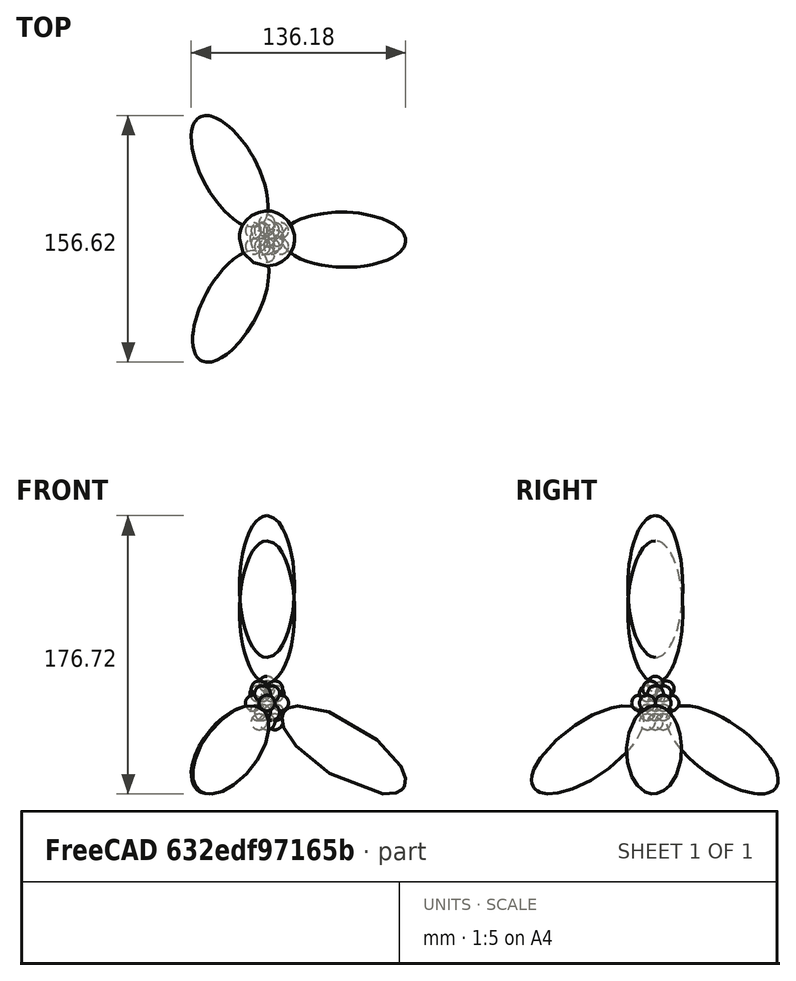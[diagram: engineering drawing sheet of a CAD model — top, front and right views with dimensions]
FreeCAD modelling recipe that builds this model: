
FCSTD DOCUMENT  (FreeCAD 0.16R6707 (Git))
Label: si-atom
License: All rights reserved
LicenseURL: http://en.wikipedia.org/wiki/All_rights_reserved
objects: Part::Feature×23, Part::Part2DObjectPython×15, Part::Sphere×9, App::DocumentObjectGroup×5, Sketcher::SketchObject×1, PartDesign::Revolution×1
note: 50 computed .brp shape members not serialized (recipe doc carries the construction recipe); baked Part::Feature solids carry a one-line shape summary decoded from their .brp

FEATURE [Part::Feature] Sphere001
  Placement = pos=(0,-10,31) rot=(0,0,1;0rad)
  shape: bbox 10 x 10 x 10 mm, 1 faces (baked)
FEATURE [Part::Feature] Sphere002
  Placement = pos=(-8.66025,-5,31) rot=(0,0,1;0rad)
  shape: bbox 10 x 10 x 10 mm, 1 faces (baked)
FEATURE [Part::Feature] Sphere003
  Placement = pos=(-8.66025,5,31) rot=(0,0,1;0rad)
  shape: bbox 10 x 10 x 10 mm, 1 faces (baked)
FEATURE [Part::Feature] Sphere004
  Placement = pos=(8.66025,-5,31) rot=(0,0,1;0rad)
  shape: bbox 10 x 10 x 10 mm, 1 faces (baked)
FEATURE [Part::Feature] Sphere005
  Placement = pos=(8.66025,5,31) rot=(0,0,1;0rad)
  shape: bbox 10 x 10 x 10 mm, 1 faces (baked)
FEATURE [Part::Feature] Sphere006
  Placement = pos=(4e-12,10,31) rot=(0,0,1;0rad)
  shape: bbox 10 x 10 x 10 mm, 1 faces (baked)
FEATURE [Part::Sphere] Sphere007
  Angle1 = -90
  Angle2 = 90
  Angle3 = 360
  Placement = pos=(0,0,31) rot=(0,0,1;0rad)
  Radius = 5
FEATURE [Part::Feature] Sphere  label="Sphere027"
  Placement = pos=(-3,5,37) rot=(0,0,1;0rad)
  shape: bbox 10 x 10 x 10 mm, 1 faces (baked)
FEATURE [Part::Feature] Sphere008  label="Sphere028"
  Placement = pos=(2.83013,5.09808,37) rot=(0,0,1;0rad)
  shape: bbox 10 x 10 x 10 mm, 1 faces (baked)
FEATURE [Part::Feature] Sphere009  label="Sphere029"
  Placement = pos=(5.83013,0.0980762,37) rot=(0,0,1;0rad)
  shape: bbox 10 x 10 x 10 mm, 1 faces (baked)
FEATURE [Part::Feature] Sphere010  label="Sphere030"
  Placement = pos=(3,-5,37) rot=(0,0,1;0rad)
  shape: bbox 10 x 10 x 10 mm, 1 faces (baked)
FEATURE [Part::Feature] Sphere011  label="Sphere031"
  Placement = pos=(-2.83013,-5.09808,37) rot=(0,0,1;0rad)
  shape: bbox 10 x 10 x 10 mm, 1 faces (baked)
FEATURE [Part::Feature] Sphere012  label="Sphere032"
  Placement = pos=(-5.83013,-0.0980762,37) rot=(0,0,1;0rad)
  shape: bbox 10 x 10 x 10 mm, 1 faces (baked)
FEATURE [Part::Feature] Sphere013  label="Sphere033"
  Placement = pos=(-3,5,25) rot=(0,0,1;0rad)
  shape: bbox 10 x 10 x 10 mm, 1 faces (baked)
FEATURE [Part::Feature] Sphere014  label="Sphere034"
  Placement = pos=(2.83013,5.09808,25) rot=(0,0,1;0rad)
  shape: bbox 10 x 10 x 10 mm, 1 faces (baked)
FEATURE [Part::Feature] Sphere015  label="Sphere035"
  Placement = pos=(-2.83013,-5.09808,25) rot=(0,0,1;0rad)
  shape: bbox 10 x 10 x 10 mm, 1 faces (baked)
FEATURE [Part::Feature] Sphere016  label="Sphere036"
  Placement = pos=(5.83013,0.0980762,25) rot=(0,0,1;0rad)
  shape: bbox 10 x 10 x 10 mm, 1 faces (baked)
FEATURE [Part::Feature] Sphere017  label="Sphere015"
  Placement = pos=(3,-5,25) rot=(0,0,1;0rad)
  shape: bbox 10 x 10 x 10 mm, 1 faces (baked)
FEATURE [Part::Feature] Sphere018  label="Sphere037"
  Placement = pos=(-5.83013,-0.0980762,25) rot=(0,0,1;0rad)
  shape: bbox 10 x 10 x 10 mm, 1 faces (baked)
FEATURE [Part::Sphere] Sphere019
  Angle1 = -90
  Angle2 = 90
  Angle3 = 360
  Placement = pos=(0,0,43) rot=(0,0,1;0rad)
  Radius = 5
FEATURE [Part::Sphere] Sphere020  label="Sphere038"
  Angle1 = -90
  Angle2 = 90
  Angle3 = 360
  Placement = pos=(0,0,19) rot=(0,0,1;0rad)
  Radius = 5
FEATURE [Part::Sphere] Sphere021  label="Sphere039"
  Angle1 = -90
  Angle2 = 90
  Angle3 = 360
  Placement = pos=(0,7,40) rot=(0,0,1;0rad)
  Radius = 5
FEATURE [Part::Sphere] Sphere022  label="Sphere040"
  Angle1 = -90
  Angle2 = 90
  Angle3 = 360
  Placement = pos=(-5,-3,40) rot=(0,0,1;0rad)
  Radius = 5
FEATURE [Part::Sphere] Sphere023  label="Sphere041"
  Angle1 = -90
  Angle2 = 90
  Angle3 = 360
  Placement = pos=(5,-3,40) rot=(0,0,1;0rad)
  Radius = 5
FEATURE [Part::Sphere] Sphere024  label="Sphere042"
  Angle1 = -90
  Angle2 = 90
  Angle3 = 360
  Placement = pos=(-5,5,19) rot=(0,0,1;0rad)
  Radius = 5
FEATURE [Part::Sphere] Sphere025  label="Sphere043"
  Angle1 = -90
  Angle2 = 90
  Angle3 = 360
  Placement = pos=(5,5,19) rot=(0,0,1;0rad)
  Radius = 5
FEATURE [Part::Sphere] Sphere026  label="Sphere044"
  Angle1 = -90
  Angle2 = 90
  Angle3 = 360
  Placement = pos=(0,-5,19) rot=(0,0,1;0rad)
  Radius = 5
FEATURE [App::DocumentObjectGroup] Group  label="core"
  Group = -> [Sphere001,Sphere002,Sphere003,Sphere004,Sphere005,Sphere006,Sphere007,Sphere,Sphere008,Sphere009,Sphere010,Sphere011,Sphere012,Sphere013,Sphere014,Sphere015,Sphere016,Sphere017,Sphere018,Sphere019,Sphere020,Sphere021,Sphere022,Sphere023,Sphere024,Sphere025,Sphere026]
FEATURE [Part::Part2DObjectPython] Polygon  # Draft 2D object (typed FeaturePython)
  ChamferSize = 0
  DrawMode = 0
  FacesNumber = 3
  FilletRadius = 0
  MakeFace = false
  Radius = 50
FEATURE [Part::Part2DObjectPython] Line  # Draft 2D object (typed FeaturePython)
  ChamferSize = 0
  Closed = false
  End = (0.452401,-0.175885,80)
  FilletRadius = 0
  Length = 80
  MakeFace = true
  Points = (2) [(0.452401,-0.175885,0),(0.452401,-0.175885,80)]
  Start = (0.452401,-0.175885,0)
  Subdivisions = 0
FEATURE [Part::Part2DObjectPython] Arc  # Draft 2D object (typed FeaturePython)
  FirstAngle = -171.133
  LastAngle = -90
  MakeFace = true
  Placement = pos=(-25,43.3013,0) rot=(0,0,1;0rad)
  Radius = 86.6025
FEATURE [Part::Part2DObjectPython] Arc001  # Draft 2D object (typed FeaturePython)
  FirstAngle = 90
  LastAngle = 169.455
  MakeFace = true
  Placement = pos=(-25,-43.3013,0) rot=(0,0,1;0rad)
  Radius = 86.6025
FEATURE [Part::Part2DObjectPython] Line001  # Draft 2D object (typed FeaturePython)
  ChamferSize = 0
  Closed = false
  End = (-25,0,0)
  FilletRadius = 0
  Length = 75
  MakeFace = true
  Points = (2) [(-100,0,0),(-25,-2.13163e-14,0)]
  Start = (-100,0,0)
  Subdivisions = 0
FEATURE [Part::Part2DObjectPython] Arc002  # Draft 2D object (typed FeaturePython)
  FirstAngle = 52.9075
  LastAngle = 180
  MakeFace = true
  Placement = pos=(-25,0,0) rot=(1,0,0;1.5708rad)
  Radius = 75
FEATURE [Part::Part2DObjectPython] Line002  # Draft 2D object (typed FeaturePython)
  ChamferSize = 0
  Closed = false
  End = (-25,-43.3013,0)
  FilletRadius = 0
  Length = 87.0816
  MakeFace = true
  Points = (2) [(1.07885,0,70.9091),(-25,-43.3013,0)]
  Start = (1.07885,0,70.9091)
  Subdivisions = 0
FEATURE [Part::Part2DObjectPython] Line003  # Draft 2D object (typed FeaturePython)
  ChamferSize = 0
  Closed = false
  End = (50,0,0)
  FilletRadius = 0
  Length = 86.1474
  MakeFace = true
  Points = (2) [(1.07885,0,70.9091),(50,1.53081e-15,0)]
  Start = (1.07885,0,70.9091)
  Subdivisions = 0
FEATURE [Part::Part2DObjectPython] Line004  # Draft 2D object (typed FeaturePython)
  ChamferSize = 0
  Closed = false
  End = (-25,43.3013,0)
  FilletRadius = 0
  Length = 87.0816
  MakeFace = true
  Points = (2) [(1.07885,0,70.9091),(-25,43.3013,0)]
  Start = (1.07885,0,70.9091)
  Subdivisions = 0
FEATURE [App::DocumentObjectGroup] Group001  label="tetrahedron"
  Group = -> [Line002,Line003,Line004,Polygon]
FEATURE [Part::Part2DObjectPython] Line006  # Draft 2D object (typed FeaturePython)
  ChamferSize = 0
  Closed = false
  End = (50,0,0)
  FilletRadius = 0
  Length = 58.8303
  MakeFace = true
  Points = (2) [(0,0,31),(50,1.53081e-15,0)]
  Start = (0,0,31)
  Subdivisions = 0
FEATURE [Part::Part2DObjectPython] Line007  # Draft 2D object (typed FeaturePython)
  ChamferSize = 0
  Closed = false
  End = (1.07885,0,70.9091)
  FilletRadius = 0
  Length = 39.9237
  MakeFace = true
  Points = (2) [(0,0,31),(1.07885,0,70.9091)]
  Start = (0,0,31)
  Subdivisions = 0
FEATURE [Part::Part2DObjectPython] Line008  # Draft 2D object (typed FeaturePython)
  ChamferSize = 0
  Closed = false
  End = (-25,43.3013,0)
  FilletRadius = 0
  Length = 58.8303
  MakeFace = true
  Points = (2) [(0,0,31),(-25,43.3013,0)]
  Start = (0,0,31)
  Subdivisions = 0
FEATURE [Sketcher::SketchObject] Sketch
  Placement = pos=(0,0,0) rot=(1,0,0;1.5708rad)
  sketch-geometry (6):
    g0: LineSegment StartX=0 StartY=60 StartZ=0 EndX=0 EndY=150 EndZ=0
    g1: ArcOfEllipse CenterX=0 CenterY=105 CenterZ=0 NormalX=0 NormalY=0 NormalZ=1 MajorRadius=45 MinorRadius=17.5 AngleXU=1.5708 StartAngle=3.14159 EndAngle=6.28319
    g2: LineSegment [constr] StartX=0 StartY=150 StartZ=0 EndX=0 EndY=60 EndZ=0
    g3: LineSegment [constr] StartX=-17.5 StartY=105 StartZ=0 EndX=17.5 EndY=105 EndZ=0
    g4: GeomPoint [constr] X=0 Y=146.458 Z=0
    g5: GeomPoint [constr] X=0 Y=63.5422 Z=0
  constraints (10):
    c: PointOnObject(g0,g-2)
    c: PointOnObject(g0,g-2)
    c: InternalAlignment(g2-g5 -> g1) x4
    c: Coincident(g2,g0)
    c: Coincident(g1,g0)
    c: Coincident(g2,g0)
    c: DistanceX(g3,g3) = 35
    c: DistanceY(g-1,g0) = 60
    c: DistanceY(g0,g0) = 90
    c: Coincident(g1,g0)
FEATURE [PartDesign::Revolution] Revolution001  label="orbital-1"
  Angle = 360
  Axis = (0,0,1)
  Base = (0,0,0)
  Placement = pos=(0,0,0) rot=(1,0,0;1.5708rad)
  ReferenceAxis = -> Sketch [V_Axis]
  Reversed = true
  Sketch = -> Sketch
FEATURE [Part::Feature] Face
  shape: bbox 40.2 x 69.18 x 91.71 mm, 1 faces, 0 solids (baked)
FEATURE [Part::Part2DObjectPython] Arc003  # Draft 2D object (typed FeaturePython)
  FirstAngle = -223.482
  LastAngle = -86.8237
  MakeFace = true
  Placement = pos=(0,0,31) rot=(-0.761669,-0.469136,0.446958;1.79277rad)
  Radius = 39.9237
FEATURE [Part::Part2DObjectPython] Line010  # Draft 2D object (typed FeaturePython)
  ChamferSize = 0
  Closed = false
  End = (68.0246,117.822,115.351)
  FilletRadius = 0
  Length = 200
  MakeFace = true
  Points = (2) [(-16.9656,-29.3853,9.96263),(68.0246,117.822,115.351)]
  Start = (-16.9656,-29.3853,9.96263)
  Subdivisions = 0
FEATURE [Part::Part2DObjectPython] Line005  # Draft 2D object (typed FeaturePython)
  ChamferSize = 0
  Closed = false
  End = (-25,-43.3013,0)
  FilletRadius = 0
  Length = 58.8303
  MakeFace = true
  Points = (2) [(0,0,31),(-25,-43.3013,0)]
  Start = (0,0,31)
  Subdivisions = 0
  Support = -> Sphere005
FEATURE [App::DocumentObjectGroup] Group002  label="Aux"
  Group = -> [Line,Arc,Arc001,Line001,Arc002,Line006,Line007,Line008,Face,Arc003,Line010,Line005]
FEATURE [App::DocumentObjectGroup] Group003  label="Orbital-src"
  Group = -> [Revolution001]
FEATURE [Part::Feature] Revolution001001  label="orbital-005"
  Placement = pos=(0,0,-16) rot=(1,0,0;1.5708rad)
  shape: bbox 35 x 35 x 90 mm, 1 faces (baked)
FEATURE [Part::Feature] Clone003  label="orbital-006"
  Placement = pos=(-65.4544,-121.45,-54.0897) rot=(0.801351,0.44296,-0.402024;0.815302rad)
  shape: bbox 48.41 x 71.09 x 55.95 mm, 1 faces (baked)
FEATURE [Part::Feature] Clone004  label="orbital-007"
  Placement = pos=(137.942,-2.53521,-54.0897) rot=(0.019523,0.459459,0.887984;1.81952rad)
  shape: bbox 78.57 x 34.89 x 55.95 mm, 1 faces (baked)
FEATURE [Part::Feature] Clone005  label="orbital-008"
  Placement = pos=(-66.7753,120.729,-54.0897) rot=(-0.321183,0.204089,0.924764;3.75111rad)
  shape: bbox 48.78 x 70.87 x 55.95 mm, 1 faces (baked)
FEATURE [App::DocumentObjectGroup] Group004  label="Orbitales"
  Group = -> [Revolution001001,Clone003,Clone004,Clone005]
